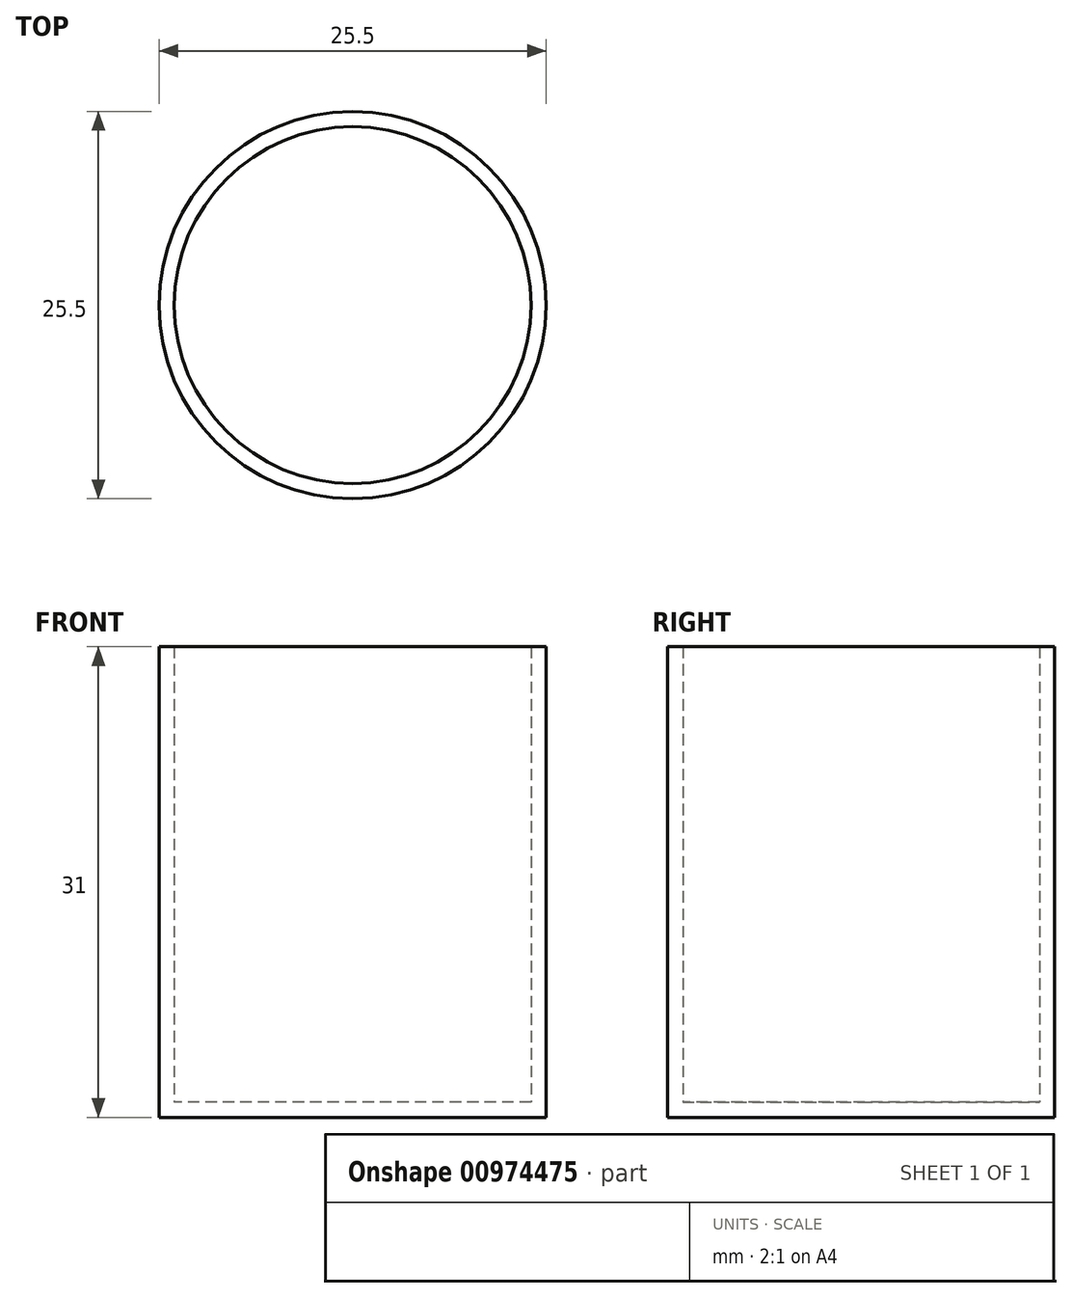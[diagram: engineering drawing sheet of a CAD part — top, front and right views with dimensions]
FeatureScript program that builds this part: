
annotation { "Feature Type Name" : "Feature", "Feature Type Description" : "" }
export const myFeature = defineFeature(function(context is Context, id is Id, definition is map)
    precondition{}
    {
        {
            var Q0;
            Q0=qCreatedBy(makeId("Top.planeOp"),FACE);
            var sketch = newSketch(context, id + "F0", { "sketchPlane" : qUnion([Q0])});
            skCircle(sketch, "E0", {"center": v(0, 0) * mm, "radius": 11.75 * mm, "construction": true});
            skCircle(sketch, "E1", {"center": v(0, 0) * mm, "radius": 12.75 * mm});
            skSolve(sketch);
        }
        {
            var Q0;
            Q0 = qSketchRegion(id + "F0", true);
            var Q1;
            Q1 = qConstructionFilter(qBodyType(qCreatedBy(id + "F0" ,EDGE), BodyType.WIRE), ConstructionObject.NO);
            extrude(context, id + "F1", {"entities" : qUnion([Q0]), "surfaceEntities" : qUnion([Q1]), "depth" : 1 * mm, "offsetDistance" : 25 * mm});
        }
        {
            var Q0;
            Q0=makeQuery(id+"F1.opExtrude","CAP_FACE",FACE,{"disambiguationData":[OSD([sQuery(id+"F0.wireOp",EDGE,"E1")])],"isStart":false});
            var sketch = newSketch(context, id + "F2", { "sketchPlane" : qUnion([Q0])});
            skCircle(sketch, "E2.0", {"center": v(0, 0) * mm, "radius": 11.75 * mm});
            skSolve(sketch);
        }
        {
            var Q0;
            Q0=makeQuery(id+"F2.imprint","IMPRINT",FACE,{"disambiguationData":[TD([[makeQuery(id+"F2.imprint","IMPRINT",EDGE,{"derivedFrom":sQuery(id+"F2.wireOp",EDGE,"E2.0")}),-1.0]])]});
            extrude(context, id + "F3", {"entities" : qUnion([Q0]), "operationType" : NewBodyOperationType.ADD, "depth" : 30 * mm, "offsetDistance" : 25 * mm});
        }
    });
